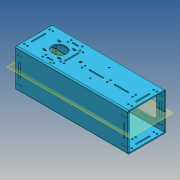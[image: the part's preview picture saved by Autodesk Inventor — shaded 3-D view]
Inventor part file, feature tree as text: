
AUTODESK INVENTOR PART (.ipt)
format: ipt  version: 2017 (Build 210142000, 142)  size: 799,232 bytes
history: native  units: mm
features: other x15, sketch x6, extrude x5, plane x1, projected_geometry x1
ambient origin geometry x8: Origin, YZ Plane, XZ Plane, XY Plane, X Axis, Y Axis, Z Axis, Center Point
bodies: Body1 (feature_tree)
feature tree (28):
  other  "Sólido1"
  extrude  "Extrusión1"  Depth=67.5mm
  other  "Pestaña1"
  sketch  "Boceto4"  dims[d9=41.14mm d10=6.0mm]
  other  "Cara1"
  other  "Cara2"
  extrude  "Extrusión4"  Depth=42.0mm
  sketch  "Boceto5"  dims[d11=53.14mm d12=6.0mm]
  other  "Cara3"
  plane  "Plano de trabajo1"
  extrude  "Extrusión5"  Depth=5.0mm
  extrude  "Extrusión3"  Depth=6.0mm
  extrude  "Extrusión2"  Depth=6.0mm
  sketch  "Boceto1"  dims[d1=56.4mm d2=67.5mm]
  sketch  "Boceto2"  dims[d4=200.0mm d5=42.0mm]
  other  "Placa1"
  other  "Doblez1"
  other  "Esquina1"
  sketch  "Boceto3"  dims[d6=8.0mm d8=5.0mm]
  projected_geometry  "Contorno proyectado1"
  other  "Placa2"
  other  "Doblez2"
  other  "Placa3"
  other  "Doblez3"
  other  "Placa4"
  other  "Doblez4"
  sketch  "Boceto6"  dims[d13=4.0mm d14=115.0mm d15=20.0mm d16=60.0mm d17=60.0mm d18=4.0mm d19=33.93mm d20=22.0mm d21=120.0mm d22=130.0mm d23=20.0mm d24=4.0mm d25=0.0mm d26=4.0mm d27=2.0mm d28=8.0mm d29=4.0mm d30=120.0mm d31=90.0deg d32=0.1mm d33=16.0mm d34=4.0mm d35=4.0mm d36=4.0mm d37=8.0mm d38=25.0mm d39=25.0mm d40=4.0mm d41=0.0mm d42=47.14mm d43=47.14mm d44=20.0mm d45=6.0mm d46=14.2mm d47=25.0mm d48=0.1mm d49=4.0mm d50=2.0mm d51=8.0mm d52=4.0mm d53=0.1mm d54=4.0mm d55=2.0mm d56=8.0mm d57=4.0mm d58=0.5mm d59=0.5mm d60=20.0mm d61=24.0mm d62=4.0mm d63=41.0mm d65=5.0mm d66=10.0mm d67=5.0mm d68=40.0mm d70=4.0mm d71=60.0mm d72=25.0mm d73=0.1mm d74=4.0mm d75=2.0mm d76=8.0mm d77=4.0mm d78=4.0mm d79=41.0mm d80=55.75mm d81=59.75mm d82=84.0mm d83=5.0mm d84=20.0mm d85=0.0mm d86=50.0mm d87=355.0mm d88=12.5mm d89=12.5mm d90=23.6mm d91=11.8mm d92=15.0mm d93=20.0mm d94=80.0mm d95=40.0mm d96=4.0mm d97=194.8mm d98=97.4mm d99=10.0mm d100=10.0mm d101=60.0mm d102=12.0mm d103=0.25mm d104=5.0mm d105=8.0mm d106=3.0mm d107=8.0mm d108=3.0mm d109=12.5mm d110=10.0mm d111=40.0mm d112=5.0mm d113=10.0mm d114=0.0mm d115=10.0mm d116=0.0mm]
  other  "Definición1"
